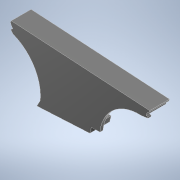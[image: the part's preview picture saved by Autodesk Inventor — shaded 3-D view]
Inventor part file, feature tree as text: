
AUTODESK INVENTOR PART (.ipt)
format: ipt  version: 2022 (Build 260153000, 153)  size: 316,416 bytes
history: native  units: in
note: dims shown in document units (in); Inventor stores cm internally (conversion verified against a paired STEP export)
features: extrude x2, sketch x2, other x1
ambient origin geometry x8: Origin, YZ Plane, XZ Plane, XY Plane, X Axis, Y Axis, Z Axis, Center Point
bodies: Body1 (feature_tree)
feature tree (5):
  other  "Sólido1"
  extrude  "Extrusión1"  Depth=0.2559in
  extrude  "Extrusión2"  Depth=0.0787in
  sketch  "Boceto1"  dims[d19=0.2559in d20=0.0in d27=0.1378in d31=0.128in]
  sketch  "Boceto2"  dims[d38=0.0394in d39=0.0in d40=0.0787in d41=0.0787in]
